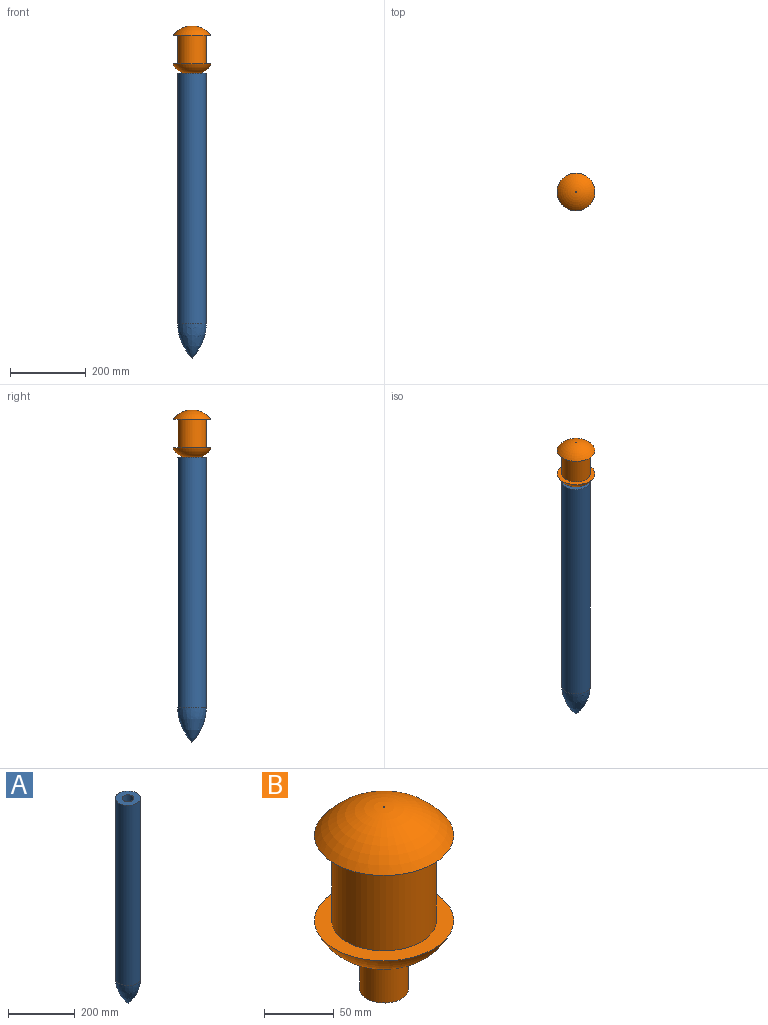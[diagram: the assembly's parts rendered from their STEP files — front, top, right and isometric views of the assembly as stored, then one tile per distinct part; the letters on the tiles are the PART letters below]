
ASSEMBLY  parts=2 mates=1
PART A: 6 faces, bbox 75x75x750 mm
  f0: cone r=0mm half-angle=45deg, axis (0,0,1), area 0.4mm2, adj f1
  f1: revolved ~89.8x75mm, area 15567.8mm2, adj f0,f3
  f2: plane 35x35mm, normal (0,0,1), area 962.1mm2, adj f4
  f3: cylinder r=37.5mm len=659.9mm, axis (0,0,1), area 155484.1mm2, adj f1,f5
  f4: cylinder r=17.5mm len=35mm, axis (0,0,1), area 3848.5mm2, adj f2,f5
  f5: plane 75x75mm, normal (0,0,1), area 3455.8mm2, adj f3,f4
PART B: 8 faces, bbox 100x100x160 mm
  f0: plane 0.5x0.5mm, normal (0,0,1), area 0.2mm2, adj f1
  f1: torus R=0.25mm, axis (0,0,1), area 9829.9mm2, adj f0,f2
  f2: plane 100x100mm, normal (0,0,-1), area 3436.1mm2, adj f1,f3
  f3: cylinder r=37.5mm len=75mm, axis (0,0,1), area 17671.5mm2, adj f2,f4
  f4: plane 100x100mm, normal (0,0,1), area 3436.1mm2, adj f3,f5
  f5: torus R=11.05mm, axis (0,0,1), area 9647mm2, adj f4,f6
  f6: cylinder r=17.5mm len=35mm, axis (0,0,1), area 3848.5mm2, adj f5,f7
  f7: plane 35x35mm, normal (0,0,-1), area 962.1mm2, adj f6
PLACE A t=(-112.6,-127.83,-369.23)mm
PLACE B t=(-112.6,-127.83,280.77)mm
MATE revolute B.f1 <-> A.f0  axis (0,0,1) through (-112.6,-127.83,280.77)mm
